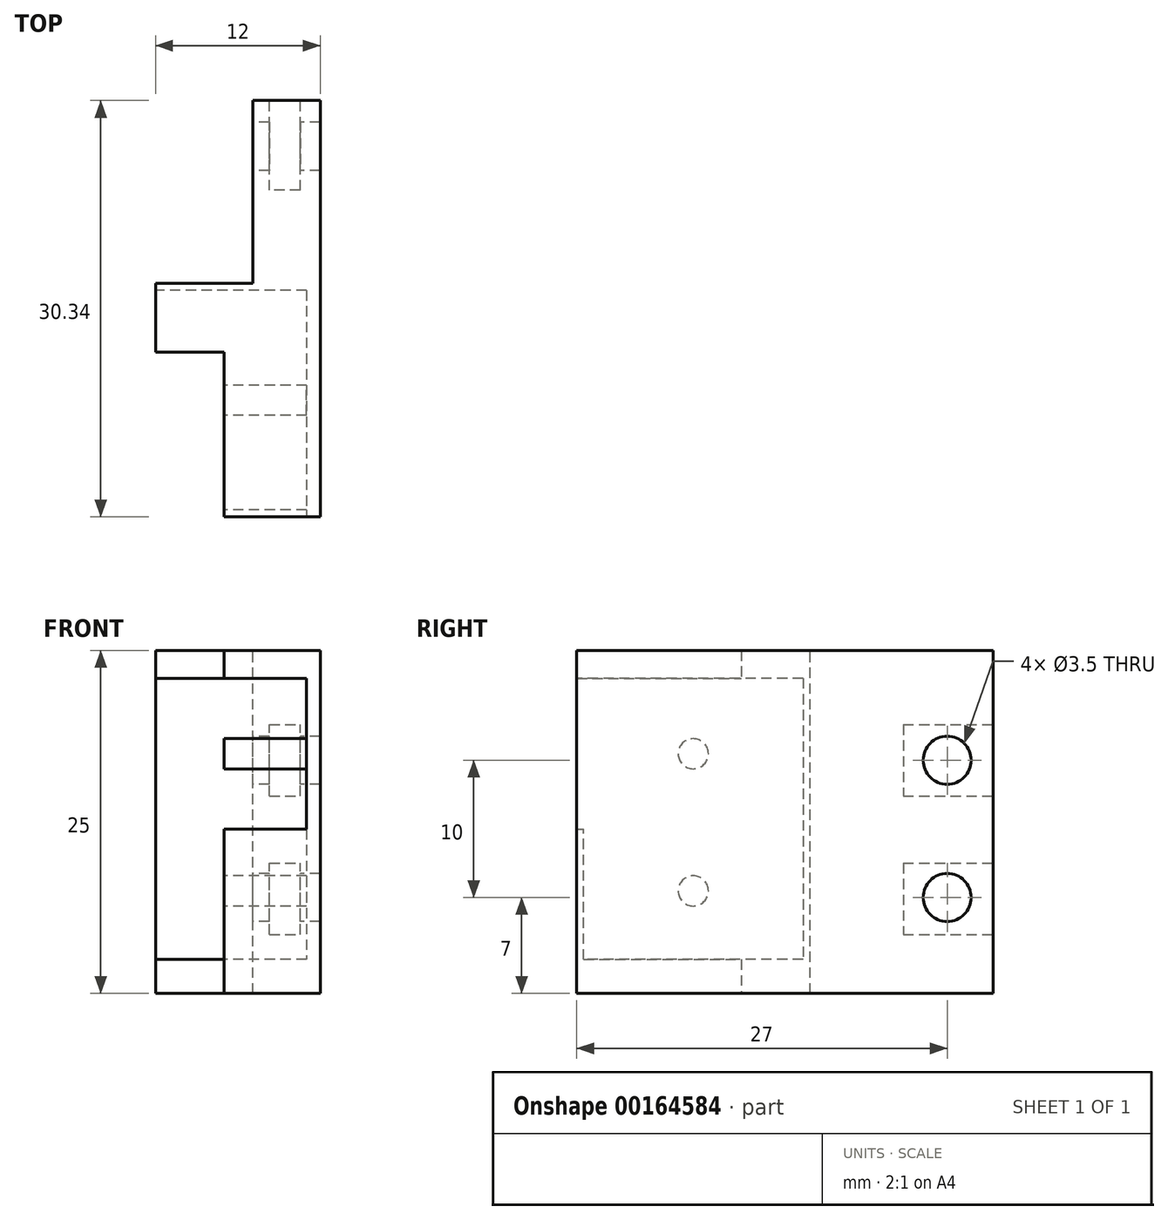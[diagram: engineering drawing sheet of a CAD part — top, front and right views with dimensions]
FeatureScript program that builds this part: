
annotation { "Feature Type Name" : "Feature", "Feature Type Description" : "" }
export const myFeature = defineFeature(function(context is Context, id is Id, definition is map)
    precondition{}
    {
        {
            var Q0;
            Q0=qCreatedBy(makeId("Top.planeOp"),FACE);
            var sketch = newSketch(context, id + "F0", { "sketchPlane" : qUnion([Q0])});
            skLineSegment(sketch, "E0.bottom", {"start": v(7.87, 15) * mm, "end": v(19.87, 15) * mm});
            skLineSegment(sketch, "E0.top", {"start": v(7.87, -17) * mm, "end": v(19.87, -17) * mm});
            skLineSegment(sketch, "E0.left", {"start": v(7.87, 15) * mm, "end": v(7.87, -17) * mm});
            skLineSegment(sketch, "E0.right", {"start": v(19.87, 15) * mm, "end": v(19.87, -17) * mm});
            skLineSegment(sketch, "E1.bottom", {"start": v(11.37, 15) * mm, "end": v(14.97, 15) * mm});
            skLineSegment(sketch, "E1.top", {"start": v(11.37, 0) * mm, "end": v(14.97, 0) * mm});
            skLineSegment(sketch, "E1.left", {"start": v(11.37, 15) * mm, "end": v(11.37, 0) * mm});
            skLineSegment(sketch, "E1.right", {"start": v(14.97, 15) * mm, "end": v(14.97, 0) * mm});
            skSolve(sketch);
        }
        {
            var Q0;
            Q0=makeQuery(id+"F0.imprint","IMPRINT",FACE,{"disambiguationData":[TD([[makeQuery(id+"F0.imprint","IMPRINT",EDGE,{"derivedFrom":sQuery(id+"F0.wireOp",EDGE,"E0.top")}),1.0]])]});
            extrude(context, id + "F1", {"entities" : qUnion([Q0]), "depth" : 25 * mm});
        }
        {
            var Q0;
            Q0=makeQuery(id+"F1.opExtrude","SWEPT_FACE",FACE,{"disambiguationData":[OSD([sQuery(id+"F0.wireOp",EDGE,"E0.left")])]});
            var sketch = newSketch(context, id + "F2", { "sketchPlane" : qUnion([Q0])});
            skCircle(sketch, "E2", {"center": v(-10, 17) * mm, "radius": 1.75 * mm});
            skCircle(sketch, "E3", {"center": v(-10, 7) * mm, "radius": 1.75 * mm});
            skSolve(sketch);
        }
        {
            var Q0;
            Q0=makeQuery(id+"F2.imprint","IMPRINT",FACE,{"disambiguationData":[TD([[makeQuery(id+"F2.imprint","IMPRINT",EDGE,{"derivedFrom":sQuery(id+"F2.wireOp",EDGE,"E2")}),1.0]])]});
            var Q1;
            Q1=makeQuery(id+"F2.imprint","IMPRINT",FACE,{"disambiguationData":[TD([[makeQuery(id+"F2.imprint","IMPRINT",EDGE,{"derivedFrom":sQuery(id+"F2.wireOp",EDGE,"E3")}),1.0]])]});
            extrude(context, id + "F3", {"entities" : qUnion([Q0, Q1]), "operationType" : NewBodyOperationType.REMOVE, "endBound" : BoundingType.THROUGH_ALL, "oppositeDirection" : true, "depth" : 25 * mm});
        }
        {
            var Q0;
            {var subQ0=sQuery(id+"F0.wireOp",EDGE,"E0.bottom");Q0=makeQuery(id+"F1.opExtrude","SWEPT_FACE",FACE,{"disambiguationData":[OSD([subQ0]),TDD([makeQuery(id+"F0.imprint","IMPRINT",EDGE,{"disambiguationData":[TD([[makeQuery(id+"F0.imprint","INTERSECT",VERTEX,{"derivedFrom":[subQ0,sQuery(id+"F0.wireOp",EDGE,"E0.right")]}),1.0]])],"derivedFrom":subQ0})])]});}
            var sketch = newSketch(context, id + "F4", { "sketchPlane" : qUnion([Q0])});
            skLineSegment(sketch, "E4.bottom", {"start": v(-18.41, 19.6) * mm, "end": v(-16.16, 19.6) * mm});
            skLineSegment(sketch, "E4.top", {"start": v(-18.41, 14.4) * mm, "end": v(-16.16, 14.4) * mm});
            skLineSegment(sketch, "E4.left", {"start": v(-18.41, 19.6) * mm, "end": v(-18.41, 14.4) * mm});
            skLineSegment(sketch, "E4.right", {"start": v(-16.16, 19.6) * mm, "end": v(-16.16, 14.4) * mm});
            skLineSegment(sketch, "E5.bottom", {"start": v(-18.41, 9.5) * mm, "end": v(-16.16, 9.5) * mm});
            skLineSegment(sketch, "E5.top", {"start": v(-18.41, 4.3) * mm, "end": v(-16.16, 4.3) * mm});
            skLineSegment(sketch, "E5.left", {"start": v(-18.41, 9.5) * mm, "end": v(-18.41, 4.3) * mm});
            skLineSegment(sketch, "E5.right", {"start": v(-16.16, 9.5) * mm, "end": v(-16.16, 4.3) * mm});
            skSolve(sketch);
        }
        {
            var Q0;
            Q0 = qSketchRegion(id + "F4", true);
            extrude(context, id + "F5", {"entities" : qUnion([Q0]), "operationType" : NewBodyOperationType.REMOVE, "oppositeDirection" : true, "depth" : 8.2 * mm});
        }
        {
            var Q0;
            Q0=makeQuery(id+"F1.opExtrude","CAP_FACE",FACE,{"disambiguationData":[OSD([sQuery(id+"F0.wireOp",EDGE,"E0.bottom"),sQuery(id+"F0.wireOp",EDGE,"E0.top"),sQuery(id+"F0.wireOp",EDGE,"E0.left"),sQuery(id+"F0.wireOp",EDGE,"E0.right"),sQuery(id+"F0.wireOp",EDGE,"E1.top"),sQuery(id+"F0.wireOp",EDGE,"E1.left"),sQuery(id+"F0.wireOp",EDGE,"E1.right")])],"isStart":false});
            var sketch = newSketch(context, id + "F6", { "sketchPlane" : qUnion([Q0])});
            skLineSegment(sketch, "E6.bottom", {"start": v(20.46, 15.34) * mm, "end": v(13.69, 15.34) * mm});
            skLineSegment(sketch, "E6.top", {"start": v(20.46, 13.34) * mm, "end": v(13.69, 13.34) * mm});
            skLineSegment(sketch, "E6.left", {"start": v(20.46, 15.34) * mm, "end": v(20.46, 13.34) * mm});
            skLineSegment(sketch, "E6.right", {"start": v(13.69, 15.34) * mm, "end": v(13.69, 13.34) * mm});
            skLineSegment(sketch, "E7.bottom", {"start": v(11.37, 0) * mm, "end": v(7, 0) * mm});
            skLineSegment(sketch, "E7.top", {"start": v(11.37, 16.57) * mm, "end": v(7, 16.57) * mm});
            skLineSegment(sketch, "E7.left", {"start": v(11.37, 0) * mm, "end": v(11.37, 16.57) * mm});
            skLineSegment(sketch, "E7.right", {"start": v(7, 0) * mm, "end": v(7, 16.57) * mm});
            skSolve(sketch);
        }
        {
            var Q0;
            Q0 = qSketchRegion(id + "F6", true);
            extrude(context, id + "F7", {"entities" : qUnion([Q0]), "operationType" : NewBodyOperationType.REMOVE, "endBound" : BoundingType.THROUGH_ALL, "oppositeDirection" : true, "depth" : 25 * mm});
        }
        {
            var Q0;
            Q0=makeQuery(id+"F1.opExtrude","SWEPT_FACE",FACE,{"disambiguationData":[OSD([sQuery(id+"F0.wireOp",EDGE,"E0.left")])]});
            var sketch = newSketch(context, id + "F8", { "sketchPlane" : qUnion([Q0])});
            skLineSegment(sketch, "E8.bottom", {"start": v(0.5, 22.97) * mm, "end": v(16.5, 22.97) * mm});
            skLineSegment(sketch, "E8.top", {"start": v(0.5, 2.47) * mm, "end": v(16.5, 2.47) * mm});
            skLineSegment(sketch, "E8.left", {"start": v(0.5, 22.97) * mm, "end": v(0.5, 2.47) * mm});
            skLineSegment(sketch, "E8.right", {"start": v(16.5, 11.97) * mm, "end": v(16.5, 2.47) * mm});
            skLineSegment(sketch, "E9.bottom", {"start": v(16.5, 22.97) * mm, "end": v(19.07, 22.97) * mm});
            skLineSegment(sketch, "E9.top", {"start": v(16.5, 11.97) * mm, "end": v(19.07, 11.97) * mm});
            skLineSegment(sketch, "E9.right", {"start": v(19.07, 22.97) * mm, "end": v(19.07, 11.97) * mm});
            skCircle(sketch, "E10", {"center": v(8.5, 17.47) * mm, "radius": 1.1 * mm});
            skCircle(sketch, "E11", {"center": v(8.5, 7.47) * mm, "radius": 1.1 * mm});
            skSolve(sketch);
        }
        {
            var Q0;
            Q0 = qSketchRegion(id + "F8", true);
            extrude(context, id + "F9", {"entities" : qUnion([Q0]), "operationType" : NewBodyOperationType.REMOVE, "oppositeDirection" : true, "depth" : 11 * mm});
        }
        {
            var Q0;
            Q0=makeQuery(id+"F1.opExtrude","SWEPT_FACE",FACE,{"disambiguationData":[OSD([sQuery(id+"F0.wireOp",EDGE,"E0.top")])]});
            var sketch = newSketch(context, id + "F10", { "sketchPlane" : qUnion([Q0])});
            skLineSegment(sketch, "E12.bottom", {"start": v(5.32, 27.97) * mm, "end": v(12.87, 27.97) * mm});
            skLineSegment(sketch, "E12.top", {"start": v(5.32, -1.84) * mm, "end": v(12.87, -1.84) * mm});
            skLineSegment(sketch, "E12.left", {"start": v(5.32, 27.97) * mm, "end": v(5.32, -1.84) * mm});
            skLineSegment(sketch, "E12.right", {"start": v(12.87, 27.97) * mm, "end": v(12.87, -1.84) * mm});
            skSolve(sketch);
        }
        {
            var Q0;
            Q0 = qSketchRegion(id + "F10", true);
            extrude(context, id + "F11", {"entities" : qUnion([Q0]), "operationType" : NewBodyOperationType.REMOVE, "oppositeDirection" : true, "depth" : 12 * mm});
        }
    });
